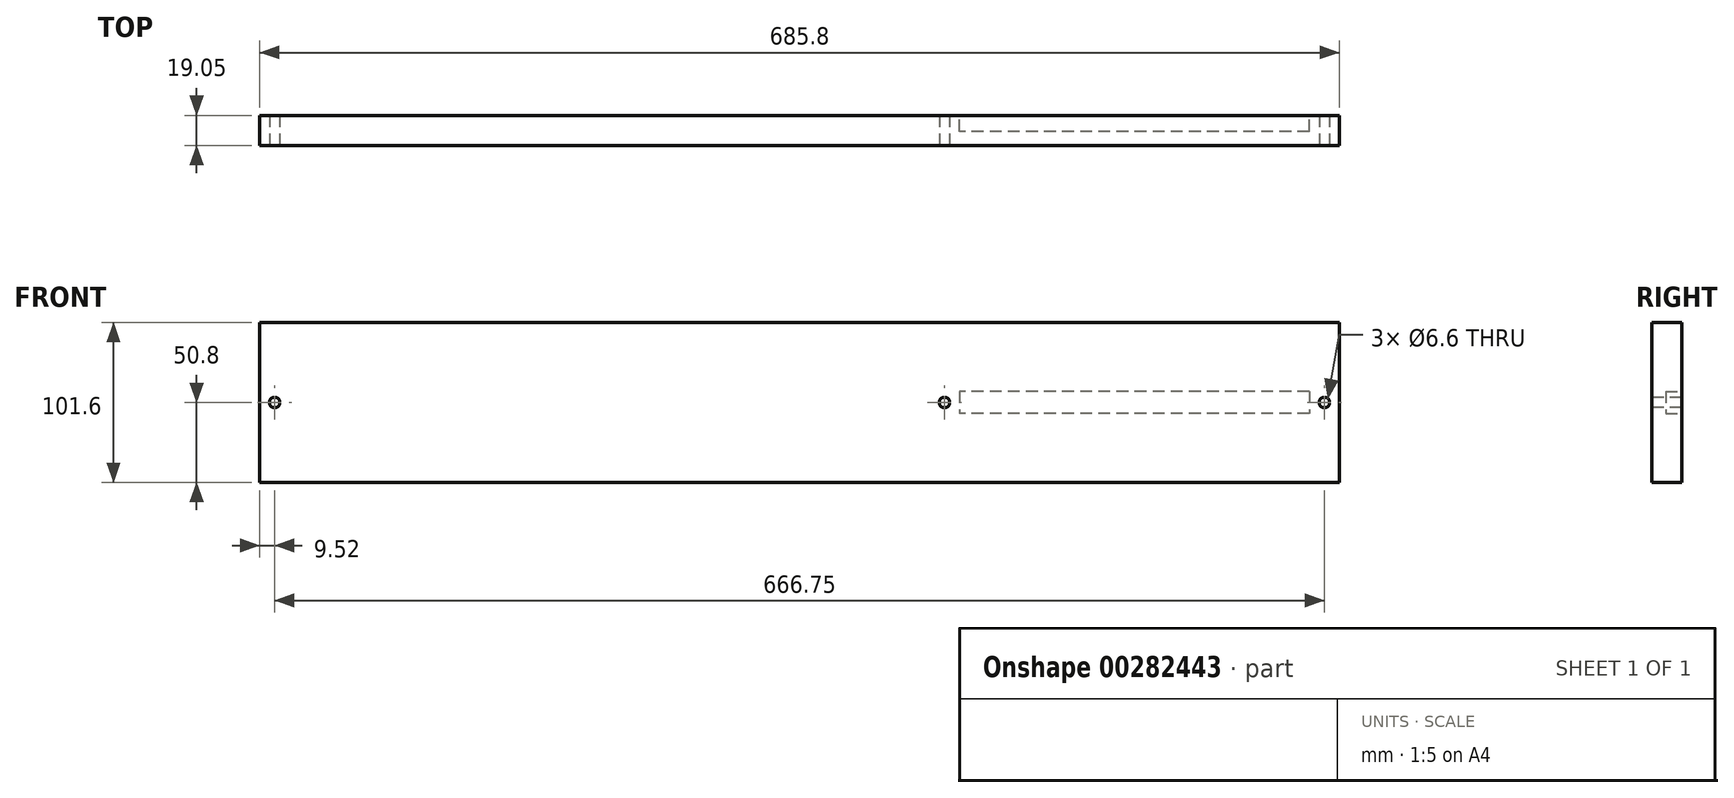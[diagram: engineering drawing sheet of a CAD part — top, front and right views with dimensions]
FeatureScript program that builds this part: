
annotation { "Feature Type Name" : "Feature", "Feature Type Description" : "" }
export const myFeature = defineFeature(function(context is Context, id is Id, definition is map)
    precondition{}
    {
        {
            var Q0;
            Q0=qCreatedBy(makeId("Front.planeOp"),FACE);
            var sketch = newSketch(context, id + "F0", { "sketchPlane" : qUnion([Q0])});
            skLineSegment(sketch, "E0.bottom", {"start": v(-297.52, 50.8) * mm, "end": v(388.28, 50.8) * mm});
            skLineSegment(sketch, "E0.top", {"start": v(-297.52, -50.8) * mm, "end": v(388.28, -50.8) * mm});
            skLineSegment(sketch, "E0.left", {"start": v(-297.52, 50.8) * mm, "end": v(-297.52, -50.8) * mm});
            skLineSegment(sketch, "E0.right", {"start": v(388.28, 50.8) * mm, "end": v(388.28, -50.8) * mm});
            skLineSegment(sketch, "E1", {"start": v(-297.52, 0) * mm, "end": v(388.28, 0) * mm, "construction": true});
            skSolve(sketch);
        }
        {
            var Q0;
            Q0=makeQuery(id+"F0.imprint","IMPRINT",FACE,{"disambiguationData":[TD([[makeQuery(id+"F0.imprint","IMPRINT",EDGE,{"derivedFrom":sQuery(id+"F0.wireOp",EDGE,"E0.bottom")}),-1.0]])]});
            extrude(context, id + "F1", {"entities" : qUnion([Q0]), "depth" : 19.05 * mm});
        }
        {
            var Q0;
            Q0=makeQuery(id+"F1.opExtrude","CAP_FACE",FACE,{"disambiguationData":[OSD([sQuery(id+"F0.wireOp",EDGE,"E0.bottom"),sQuery(id+"F0.wireOp",EDGE,"E0.top"),sQuery(id+"F0.wireOp",EDGE,"E0.left"),sQuery(id+"F0.wireOp",EDGE,"E0.right")])],"isStart":true});
            var sketch = newSketch(context, id + "F2", { "sketchPlane" : qUnion([Q0])});
            skLineSegment(sketch, "E2", {"start": v(-388.28, 0) * mm, "end": v(297.52, 0) * mm, "construction": true});
            skLineSegment(sketch, "E3", {"start": v(-388.28, 22.49) * mm, "end": v(-369.23, 22.49) * mm, "construction": true});
            skLineSegment(sketch, "E4", {"start": v(-369.23, 50.8) * mm, "end": v(-369.23, -50.8) * mm, "construction": true});
            skLineSegment(sketch, "E5", {"start": v(-369.23, -25) * mm, "end": v(-144.23, -25) * mm, "construction": true});
            skLineSegment(sketch, "E6", {"start": v(-144.23, 50.8) * mm, "end": v(-144.23, -50.8) * mm, "construction": true});
            skLineSegment(sketch, "E7", {"start": v(-144.23, 26.08) * mm, "end": v(-125.19, 25.41) * mm, "construction": true});
            skLineSegment(sketch, "E8", {"start": v(297.52, 15.3) * mm, "end": v(278.47, 15.3) * mm, "construction": true});
            skPoint(sketch, "E9.firstSnap0", {"position": v(-127.94, 0) * mm});
            skLineSegment(sketch, "E10", {"start": v(-127.94, 0) * mm, "end": v(278.46, 0) * mm, "construction": true});
            skLineSegment(sketch, "E11.bottom", {"start": v(-369.23, 7.05) * mm, "end": v(-146.98, 7.05) * mm});
            skLineSegment(sketch, "E11.top", {"start": v(-369.23, -7.05) * mm, "end": v(-146.98, -7.05) * mm});
            skLineSegment(sketch, "E11.left", {"start": v(-369.23, 7.05) * mm, "end": v(-369.23, -7.05) * mm});
            skLineSegment(sketch, "E11.right", {"start": v(-146.98, 7.05) * mm, "end": v(-146.98, -7.05) * mm});
            skLineSegment(sketch, "E12", {"start": v(-369.23, 0) * mm, "end": v(-146.98, 0) * mm, "construction": true});
            skSolve(sketch);
        }
        {
            var Q0;
            Q0 = qSketchRegion(id + "F2", true);
            extrude(context, id + "F3", {"entities" : qUnion([Q0]), "operationType" : NewBodyOperationType.REMOVE, "oppositeDirection" : true, "depth" : 10.16 * mm});
        }
        {
            var Q0;
            Q0=makeQuery(id+"F1.opExtrude","CAP_FACE",FACE,{"disambiguationData":[OSD([sQuery(id+"F0.wireOp",EDGE,"E0.bottom"),sQuery(id+"F0.wireOp",EDGE,"E0.top"),sQuery(id+"F0.wireOp",EDGE,"E0.left"),sQuery(id+"F0.wireOp",EDGE,"E0.right")])],"isStart":false});
            var sketch = newSketch(context, id + "F4", { "sketchPlane" : qUnion([Q0])});
            skLineSegment(sketch, "E13.0", {"start": v(388.28, 50.8) * mm, "end": v(388.28, -50.8) * mm, "construction": true});
            skLineSegment(sketch, "E13.1", {"start": v(-297.52, -50.8) * mm, "end": v(388.28, -50.8) * mm, "construction": true});
            skLineSegment(sketch, "E13.2", {"start": v(-297.52, 50.8) * mm, "end": v(388.28, 50.8) * mm, "construction": true});
            skLineSegment(sketch, "E13.3", {"start": v(-297.52, 50.8) * mm, "end": v(-297.52, -50.8) * mm, "construction": true});
            skLineSegment(sketch, "E14", {"start": v(388.28, -18.63) * mm, "end": v(369.23, -18.63) * mm, "construction": true});
            skLineSegment(sketch, "E15", {"start": v(369.23, -18.63) * mm, "end": v(146.98, -18.63) * mm, "construction": true});
            skLineSegment(sketch, "E16", {"start": v(146.98, -18.63) * mm, "end": v(127.93, -18.63) * mm, "construction": true});
            skLineSegment(sketch, "E17", {"start": v(127.93, -18.63) * mm, "end": v(-278.47, -18.63) * mm, "construction": true});
            skLineSegment(sketch, "E18", {"start": v(-278.47, -18.63) * mm, "end": v(-297.52, -18.63) * mm, "construction": true});
            skLineSegment(sketch, "E19", {"start": v(-278.47, -50.8) * mm, "end": v(-278.47, 50.8) * mm, "construction": true});
            skLineSegment(sketch, "E20", {"start": v(146.98, -50.8) * mm, "end": v(146.98, 50.8) * mm, "construction": true});
            skLineSegment(sketch, "E21", {"start": v(127.93, -50.8) * mm, "end": v(127.93, 50.8) * mm, "construction": true});
            skLineSegment(sketch, "E22", {"start": v(369.23, -50.8) * mm, "end": v(369.23, 50.8) * mm, "construction": true});
            skLineSegment(sketch, "E23", {"start": v(388.28, 0) * mm, "end": v(-297.52, 0) * mm, "construction": true});
            skLineSegment(sketch, "E24", {"start": v(-288, 50.8) * mm, "end": v(-288, 0) * mm, "construction": true});
            skPoint(sketch, "E24.startSnap0", {"position": v(-288, -18.63) * mm});
            skLineSegment(sketch, "E25", {"start": v(-288, 0) * mm, "end": v(-288, -50.8) * mm, "construction": true});
            skLineSegment(sketch, "E26", {"start": v(-278.47, -25.4) * mm, "end": v(-297.52, -25.4) * mm, "construction": true});
            skLineSegment(sketch, "E27", {"start": v(-278.47, 25.4) * mm, "end": v(-297.52, 25.4) * mm, "construction": true});
            skLineSegment(sketch, "E28", {"start": v(137.45, -50.8) * mm, "end": v(137.45, 0) * mm, "construction": true});
            skPoint(sketch, "E28.startSnap0", {"position": v(137.45, -18.63) * mm});
            skLineSegment(sketch, "E29", {"start": v(137.45, 0) * mm, "end": v(137.45, 50.8) * mm, "construction": true});
            skLineSegment(sketch, "E30", {"start": v(146.98, 25.4) * mm, "end": v(127.93, 25.4) * mm, "construction": true});
            skPoint(sketch, "E30.startSnap0", {"position": v(137.45, 25.4) * mm});
            skLineSegment(sketch, "E31", {"start": v(146.98, -25.4) * mm, "end": v(127.93, -25.4) * mm, "construction": true});
            skPoint(sketch, "E31.startSnap0", {"position": v(137.45, -25.4) * mm});
            skLineSegment(sketch, "E32", {"start": v(378.75, 50.8) * mm, "end": v(378.75, 0) * mm});
            skPoint(sketch, "E32.startSnap0", {"position": v(378.75, -18.63) * mm});
            skLineSegment(sketch, "E33", {"start": v(378.75, 0) * mm, "end": v(378.75, -50.8) * mm});
            skLineSegment(sketch, "E34", {"start": v(388.28, -25.4) * mm, "end": v(369.23, -25.4) * mm});
            skPoint(sketch, "E34.startSnap0", {"position": v(378.75, -25.4) * mm});
            skLineSegment(sketch, "E35", {"start": v(388.28, 25.4) * mm, "end": v(369.23, 25.4) * mm, "construction": true});
            skPoint(sketch, "E35.startSnap0", {"position": v(378.75, 25.4) * mm});
            skCircle(sketch, "E36", {"center": v(378.75, 0) * mm, "radius": 3.3 * mm});
            skCircle(sketch, "E37", {"center": v(137.45, 0) * mm, "radius": 3.3 * mm});
            skCircle(sketch, "E38", {"center": v(-288, 0) * mm, "radius": 3.3 * mm});
            skLineSegment(sketch, "E39", {"start": v(137.45, 50.8) * mm, "end": v(137.45, 0) * mm, "construction": true});
            skSolve(sketch);
        }
        {
            var Q0;
            Q0 = qSketchRegion(id + "F4", true);
            extrude(context, id + "F5", {"entities" : qUnion([Q0]), "operationType" : NewBodyOperationType.REMOVE, "oppositeDirection" : true, "depth" : 25.4 * mm});
        }
    });
